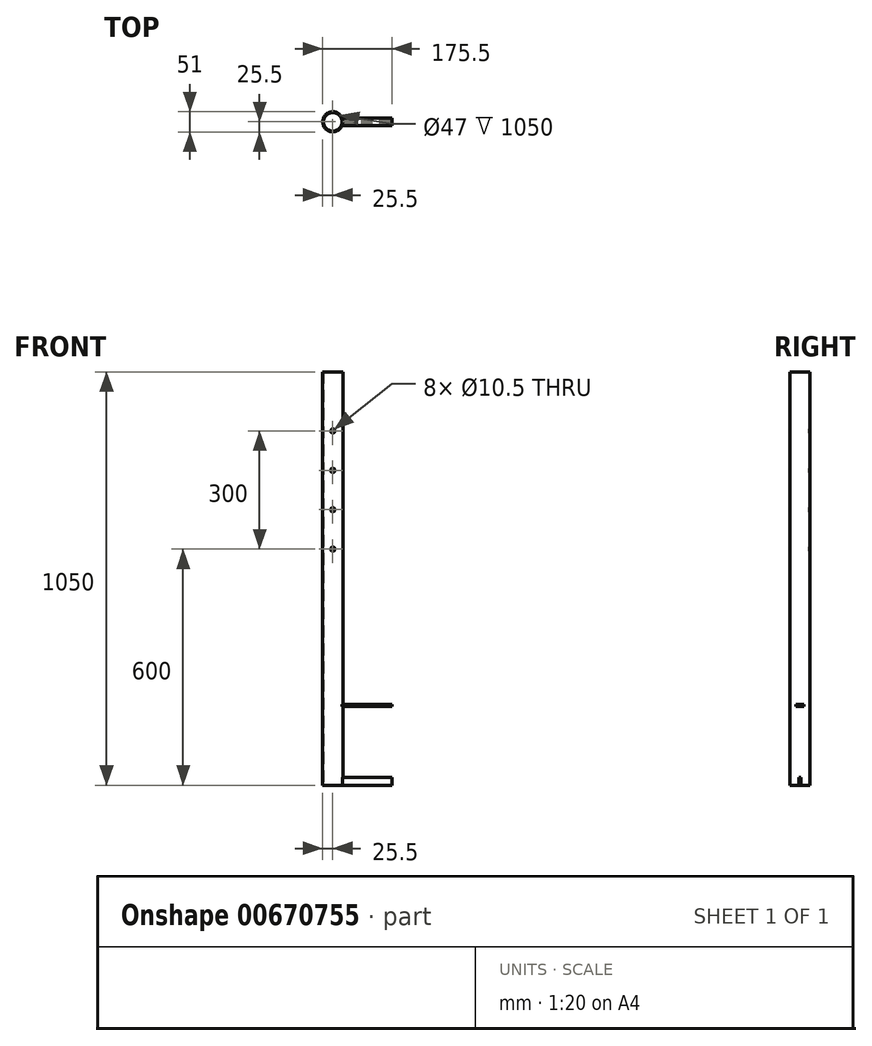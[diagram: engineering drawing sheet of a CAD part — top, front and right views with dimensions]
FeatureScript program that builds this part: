
annotation { "Feature Type Name" : "Feature", "Feature Type Description" : "" }
export const myFeature = defineFeature(function(context is Context, id is Id, definition is map)
    precondition{}
    {
        {
            var Q0;
            Q0=qCreatedBy(makeId("Top.planeOp"),FACE);
            var sketch = newSketch(context, id + "F0", { "sketchPlane" : qUnion([Q0])});
            skCircle(sketch, "E0", {"center": v(0, 0) * mm, "radius": 25.5 * mm});
            skCircle(sketch, "E1", {"center": v(0, 0) * mm, "radius": 23.5 * mm});
            skSolve(sketch);
        }
        {
            var Q0;
            Q0 = qSketchRegion(id + "F0", true);
            extrude(context, id + "F1", {"entities" : qUnion([Q0]), "depth" : 1050 * mm, "offsetDistance" : 25 * mm});
        }
        {
            var Q0;
            Q0=qCreatedBy(makeId("Right.planeOp"),FACE);
            cPlane(context, id + "F2", {"entities" : qUnion([Q0]), "cplaneType" : CPlaneType.OFFSET, "offset" : 150 * mm, "width" : 150 * mm, "height" : 150 * mm});
        }
        {
            var Q0;
            Q0=qCreatedBy(id+"F2.planeOp",FACE);
            var sketch = newSketch(context, id + "F3", { "sketchPlane" : qUnion([Q0])});
            skLineSegment(sketch, "E2.bottom", {"start": v(-2.5, 0) * mm, "end": v(2.5, 0) * mm});
            skLineSegment(sketch, "E2.top", {"start": v(-2.5, 20) * mm, "end": v(2.5, 20) * mm});
            skLineSegment(sketch, "E2.left", {"start": v(-2.5, 0) * mm, "end": v(-2.5, 20) * mm});
            skLineSegment(sketch, "E2.right", {"start": v(2.5, 0) * mm, "end": v(2.5, 20) * mm});
            skLineSegment(sketch, "E3.bottom", {"start": v(-10, 205) * mm, "end": v(10, 205) * mm});
            skLineSegment(sketch, "E3.top", {"start": v(-10, 200) * mm, "end": v(10, 200) * mm});
            skLineSegment(sketch, "E3.left", {"start": v(-10, 205) * mm, "end": v(-10, 200) * mm});
            skLineSegment(sketch, "E3.right", {"start": v(10, 205) * mm, "end": v(10, 200) * mm});
            skSolve(sketch);
        }
        {
            var Q0;
            Q0 = qSketchRegion(id + "F3", true);
            extrude(context, id + "F4", {"entities" : qUnion([Q0]), "operationType" : NewBodyOperationType.ADD, "endBound" : BoundingType.UP_TO_NEXT, "oppositeDirection" : true, "depth" : 25 * mm, "offsetDistance" : 25 * mm});
        }
        {
            var Q0;
            Q0=qCreatedBy(makeId("Front.planeOp"),FACE);
            var sketch = newSketch(context, id + "F5", { "sketchPlane" : qUnion([Q0])});
            skCircle(sketch, "E4", {"center": v(0, 600) * mm, "radius": 5.25 * mm});
            skCircle(sketch, "E5", {"center": v(0, 700) * mm, "radius": 5.25 * mm});
            skCircle(sketch, "E6", {"center": v(0, 800) * mm, "radius": 5.25 * mm});
            skCircle(sketch, "E7", {"center": v(0, 900) * mm, "radius": 5.25 * mm});
            skSolve(sketch);
        }
        {
            var Q0;
            Q0 = qSketchRegion(id + "F5", true);
            extrude(context, id + "F6", {"entities" : qUnion([Q0]), "operationType" : NewBodyOperationType.REMOVE, "endBound" : BoundingType.THROUGH_ALL, "oppositeDirection" : true, "depth" : 25 * mm, "offsetDistance" : 25 * mm, "hasSecondDirection" : true, "secondDirectionBound" : SecondDirectionBoundingType.THROUGH_ALL, "secondDirectionOppositeDirection" : false, "secondDirectionDepth" : 25 * mm});
        }
    });
